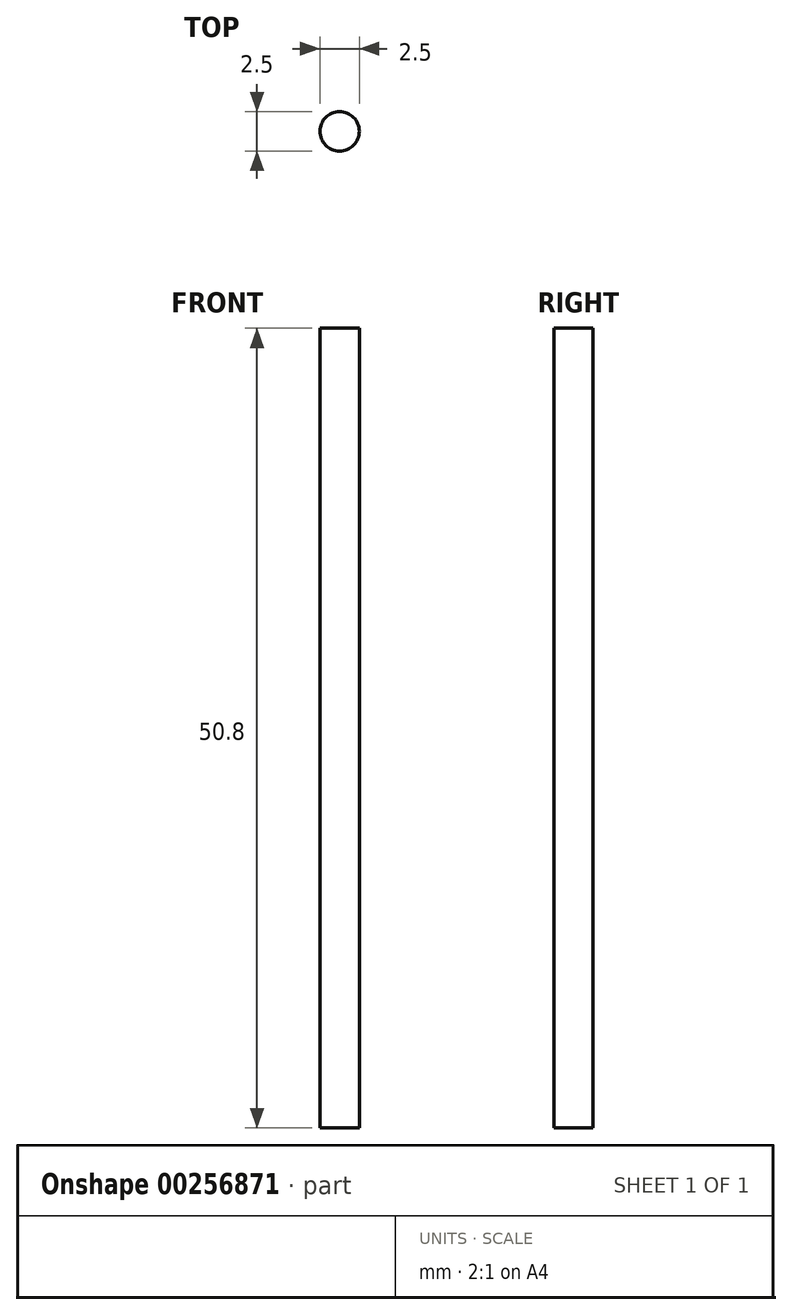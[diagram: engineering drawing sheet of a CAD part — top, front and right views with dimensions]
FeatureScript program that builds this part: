
annotation { "Feature Type Name" : "Feature", "Feature Type Description" : "" }
export const myFeature = defineFeature(function(context is Context, id is Id, definition is map)
    precondition{}
    {
        {
            var Q0;
            Q0=qCreatedBy(makeId("Top.planeOp"),FACE);
            var sketch = newSketch(context, id + "F0", { "sketchPlane" : qUnion([Q0])});
            skCircle(sketch, "E0", {"center": v(0, 0) * mm, "radius": 1.25 * mm});
            skSolve(sketch);
        }
        {
            var Q0;
            Q0 = qSketchRegion(id + "F0", true);
            extrude(context, id + "F1", {"entities" : qUnion([Q0]), "depth" : 50.8 * mm});
        }
    });
